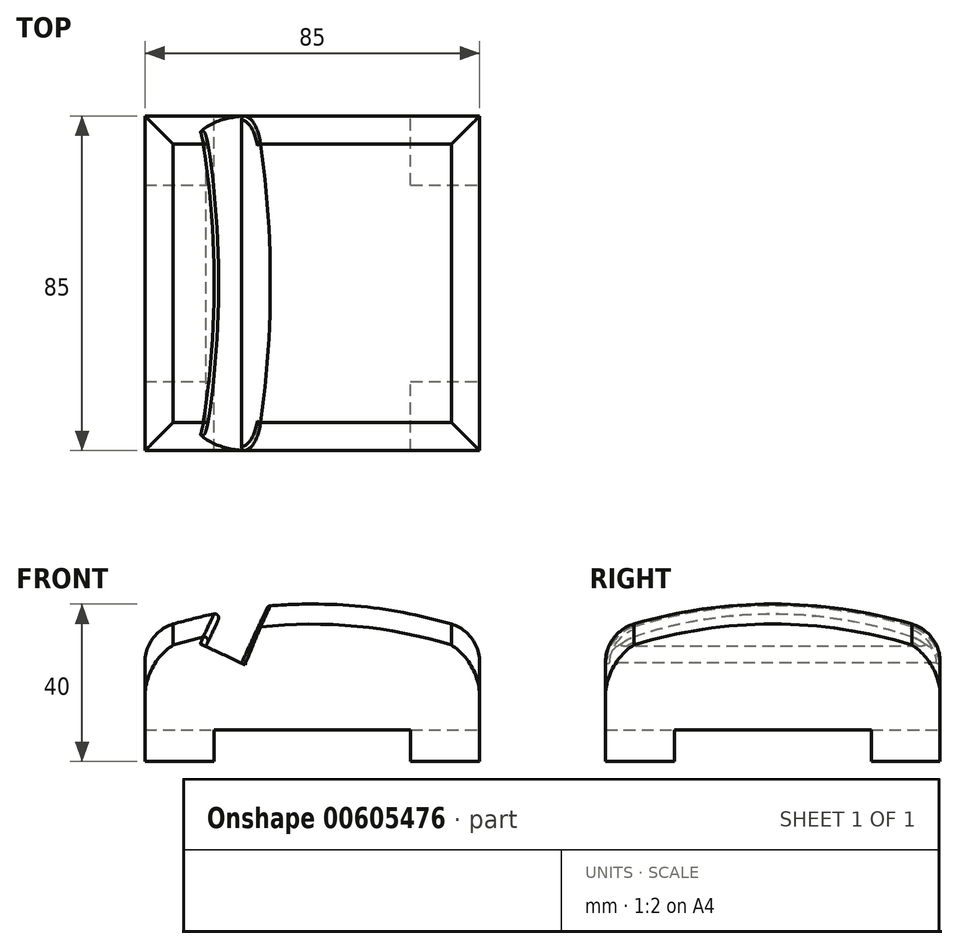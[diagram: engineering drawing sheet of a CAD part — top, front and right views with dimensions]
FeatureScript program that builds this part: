
annotation { "Feature Type Name" : "Feature", "Feature Type Description" : "" }
export const myFeature = defineFeature(function(context is Context, id is Id, definition is map)
    precondition{}
    {
        {
            var Q0;
            Q0=qCreatedBy(makeId("Front.planeOp"),FACE);
            var sketch = newSketch(context, id + "F0", { "sketchPlane" : qUnion([Q0])});
            skArc(sketch, "E0", {"start": v(91.65, 0) * mm, "mid": v(50, 29.56) * mm, "end": v(0, 40) * mm});
            skLineSegment(sketch, "E1", {"start": v(0, 0) * mm, "end": v(91.65, 0) * mm});
            skLineSegment(sketch, "E2", {"start": v(0, 0) * mm, "end": v(0, 40) * mm});
            skPoint(sketch, "E3.orphan", {"position": v(-91.65, 0) * mm});
            skSolve(sketch);
        }
        {
            var Q0;
            Q0=makeQuery(id+"F0.imprint","IMPRINT",FACE,{"disambiguationData":[TD([[makeQuery(id+"F0.imprint","IMPRINT",EDGE,{"derivedFrom":sQuery(id+"F0.wireOp",EDGE,"E0")}),1.0]])]});
            var Q1;
            Q1=sQuery(id+"F0.wireOp",EDGE,"E2");
            revolve(context, id + "F1", {"entities" : qUnion([Q0]), "axis" : qUnion([Q1]), "revolveType" : RevolveType.FULL});
        }
        {
            var Q0;
            Q0=qCreatedBy(makeId("Top.planeOp"),FACE);
            var sketch = newSketch(context, id + "F2", { "sketchPlane" : qUnion([Q0])});
            skLineSegment(sketch, "E4.bottom", {"start": v(-42.5, 42.5) * mm, "end": v(42.5, 42.5) * mm});
            skLineSegment(sketch, "E4.top", {"start": v(-42.5, -42.5) * mm, "end": v(42.5, -42.5) * mm});
            skLineSegment(sketch, "E4.left", {"start": v(-42.5, 42.5) * mm, "end": v(-42.5, -42.5) * mm});
            skLineSegment(sketch, "E4.right", {"start": v(42.5, 42.5) * mm, "end": v(42.5, -42.5) * mm});
            skSolve(sketch);
        }
        {
            var Q0;
            Q0=makeQuery(id+"F2.imprint","IMPRINT",FACE,{"disambiguationData":[TD([[makeQuery(id+"F2.imprint","IMPRINT",EDGE,{"derivedFrom":sQuery(id+"F2.wireOp",EDGE,"E4.bottom")}),-1.0]])]});
            extrude(context, id + "F3", {"entities" : qUnion([Q0]), "operationType" : NewBodyOperationType.INTERSECT, "endBound" : BoundingType.THROUGH_ALL, "depth" : 25 * mm, "offsetDistance" : 25 * mm});
        }
        {
            var Q0;
            Q0=makeQuery(id+"F3.boolean.opBoolean","INTERSECT",EDGE,{"derivedFrom":[makeQuery(id+"F1.opRevolve","SWEPT_FACE",FACE,{"disambiguationData":[OSD([sQuery(id+"F0.wireOp",EDGE,"E0")])]}),makeQuery(id+"F3.boolean.toolComplement.opBoolean","COPY",FACE,{"derivedFrom":makeQuery(id+"F3.opExtrude","SWEPT_FACE",FACE,{"disambiguationData":[OSD([sQuery(id+"F2.wireOp",EDGE,"E4.top")])]})})]});
            var Q1;
            Q1=makeQuery(id+"F1.opRevolve","SWEPT_FACE",FACE,{"disambiguationData":[OSD([sQuery(id+"F0.wireOp",EDGE,"E0")])]});
            var Q2;
            Q2=makeQuery(id+"F3.boolean.opBoolean","COPY",EDGE,{"derivedFrom":makeQuery(id+"F3.boolean.toolComplement.opBoolean","COPY",EDGE,{"derivedFrom":makeQuery(id+"F3.opExtrude","SWEPT_EDGE",EDGE,{"disambiguationData":[OSD([sQuery(id+"F2.wireOp",EDGE,"E4.top"),sQuery(id+"F2.wireOp",EDGE,"E4.right")])]})})});
            var Q3;
            Q3=makeQuery(id+"F3.boolean.opBoolean","COPY",EDGE,{"derivedFrom":makeQuery(id+"F3.boolean.toolComplement.opBoolean","COPY",EDGE,{"derivedFrom":makeQuery(id+"F3.opExtrude","SWEPT_EDGE",EDGE,{"disambiguationData":[OSD([sQuery(id+"F2.wireOp",EDGE,"E4.bottom"),sQuery(id+"F2.wireOp",EDGE,"E4.right")])]})})});
            var Q4;
            Q4=makeQuery(id+"F3.boolean.opBoolean","COPY",EDGE,{"derivedFrom":makeQuery(id+"F3.boolean.toolComplement.opBoolean","COPY",EDGE,{"derivedFrom":makeQuery(id+"F3.opExtrude","SWEPT_EDGE",EDGE,{"disambiguationData":[OSD([sQuery(id+"F2.wireOp",EDGE,"E4.top"),sQuery(id+"F2.wireOp",EDGE,"E4.left")])]})})});
            var Q5;
            Q5=makeQuery(id+"F3.boolean.opBoolean","COPY",EDGE,{"derivedFrom":makeQuery(id+"F3.boolean.toolComplement.opBoolean","COPY",EDGE,{"derivedFrom":makeQuery(id+"F3.opExtrude","SWEPT_EDGE",EDGE,{"disambiguationData":[OSD([sQuery(id+"F2.wireOp",EDGE,"E4.bottom"),sQuery(id+"F2.wireOp",EDGE,"E4.left")])]})})});
            fillet(context, id + "F4", {"entities" : qUnion([Q0, Q1, Q2, Q3, Q4, Q5]), "radius" : 10 * mm, "tangentPropagation" : true, "allowEdgeOverflow" : false});
        }
        {
            var Q0;
            Q0=qCreatedBy(makeId("Front.planeOp"),FACE);
            var sketch = newSketch(context, id + "F5", { "sketchPlane" : qUnion([Q0])});
            skLineSegment(sketch, "E5", {"start": v(-9.66, 66.55) * mm, "end": v(-27.06, 29.23) * mm});
            skLineSegment(sketch, "E6", {"start": v(-27.06, 29.23) * mm, "end": v(-18, 25) * mm});
            skLineSegment(sketch, "E7", {"start": v(-18, 25) * mm, "end": v(15.05, 95.88) * mm});
            skLineSegment(sketch, "E8", {"start": v(15.05, 95.88) * mm, "end": v(-9.66, 66.55) * mm});
            skSolve(sketch);
        }
        {
            var Q0;
            Q0=makeQuery(id+"F5.imprint","IMPRINT",FACE,{"disambiguationData":[TD([[makeQuery(id+"F5.imprint","IMPRINT",EDGE,{"derivedFrom":sQuery(id+"F5.wireOp",EDGE,"E5")}),1.0]])]});
            extrude(context, id + "F6", {"entities" : qUnion([Q0]), "operationType" : NewBodyOperationType.REMOVE, "endBound" : BoundingType.THROUGH_ALL, "oppositeDirection" : true, "depth" : 25 * mm, "offsetDistance" : 25 * mm, "hasSecondDirection" : true, "secondDirectionBound" : BoundingType.THROUGH_ALL, "secondDirectionOppositeDirection" : false, "secondDirectionDepth" : 25 * mm});
        }
        {
            var Q0;
            Q0=qCreatedBy(makeId("Top.planeOp"),FACE);
            var sketch = newSketch(context, id + "F7", { "sketchPlane" : qUnion([Q0])});
            skLineSegment(sketch, "E9.bottom", {"start": v(-46.76, -25) * mm, "end": v(-25, -25) * mm});
            skLineSegment(sketch, "E9.top", {"start": v(-46.76, 25) * mm, "end": v(-25, 25) * mm});
            skLineSegment(sketch, "E9.left", {"start": v(-46.76, -25) * mm, "end": v(-46.76, 25) * mm});
            skLineSegment(sketch, "E9.right", {"start": v(49.23, -25) * mm, "end": v(49.23, 25) * mm});
            skLineSegment(sketch, "E10.bottom", {"start": v(-25, -52.45) * mm, "end": v(25, -52.45) * mm});
            skLineSegment(sketch, "E10.top", {"start": v(-25, 44.2) * mm, "end": v(25, 44.2) * mm});
            skLineSegment(sketch, "E10.left", {"start": v(-25, -52.45) * mm, "end": v(-25, -25) * mm});
            skLineSegment(sketch, "E10.right", {"start": v(25, -52.45) * mm, "end": v(25, -25) * mm});
            skLineSegment(sketch, "E11.trimOffspring", {"start": v(25, -25) * mm, "end": v(49.23, -25) * mm});
            skLineSegment(sketch, "E12.trimOffspring", {"start": v(-25, 25) * mm, "end": v(-25, 44.2) * mm});
            skLineSegment(sketch, "E13.trimOffspring", {"start": v(25, 25) * mm, "end": v(49.23, 25) * mm});
            skLineSegment(sketch, "E14.trimOffspring", {"start": v(25, 25) * mm, "end": v(25, 44.2) * mm});
            skSolve(sketch);
        }
        {
            var Q0;
            Q0=makeQuery(id+"F7.imprint","IMPRINT",FACE,{"disambiguationData":[TD([[makeQuery(id+"F7.imprint","IMPRINT",EDGE,{"derivedFrom":sQuery(id+"F7.wireOp",EDGE,"E9.bottom")}),1.0]])]});
            extrude(context, id + "F8", {"entities" : qUnion([Q0]), "operationType" : NewBodyOperationType.REMOVE, "depth" : 8 * mm, "offsetDistance" : 25 * mm});
        }
        {
            var Q0;
            Q0=makeQuery(id+"F6.boolean.opBoolean","INTERSECT",EDGE,{"derivedFrom":[makeQuery(id+"F1.opRevolve","SWEPT_FACE",FACE,{"disambiguationData":[OSD([sQuery(id+"F0.wireOp",EDGE,"E0")])]}),makeQuery(id+"F6.opExtrude","SWEPT_FACE",FACE,{"disambiguationData":[OSD([sQuery(id+"F5.wireOp",EDGE,"E5")])]})]});
            var Q1;
            Q1=makeQuery(id+"F6.boolean.opBoolean","INTERSECT",EDGE,{"derivedFrom":[makeQuery(id+"F4.opFillet","BLEND_FACE",FACE,{"disambiguationData":[OSD([sQuery(id+"F0.wireOp",EDGE,"E0"),sQuery(id+"F2.wireOp",EDGE,"E4.top")])]}),makeQuery(id+"F6.opExtrude","SWEPT_FACE",FACE,{"disambiguationData":[OSD([sQuery(id+"F5.wireOp",EDGE,"E7")])]})]});
            fillet(context, id + "F9", {"entities" : qUnion([Q0, Q1]), "radius" : 1 * mm, "tangentPropagation" : true, "allowEdgeOverflow" : false});
        }
    });
